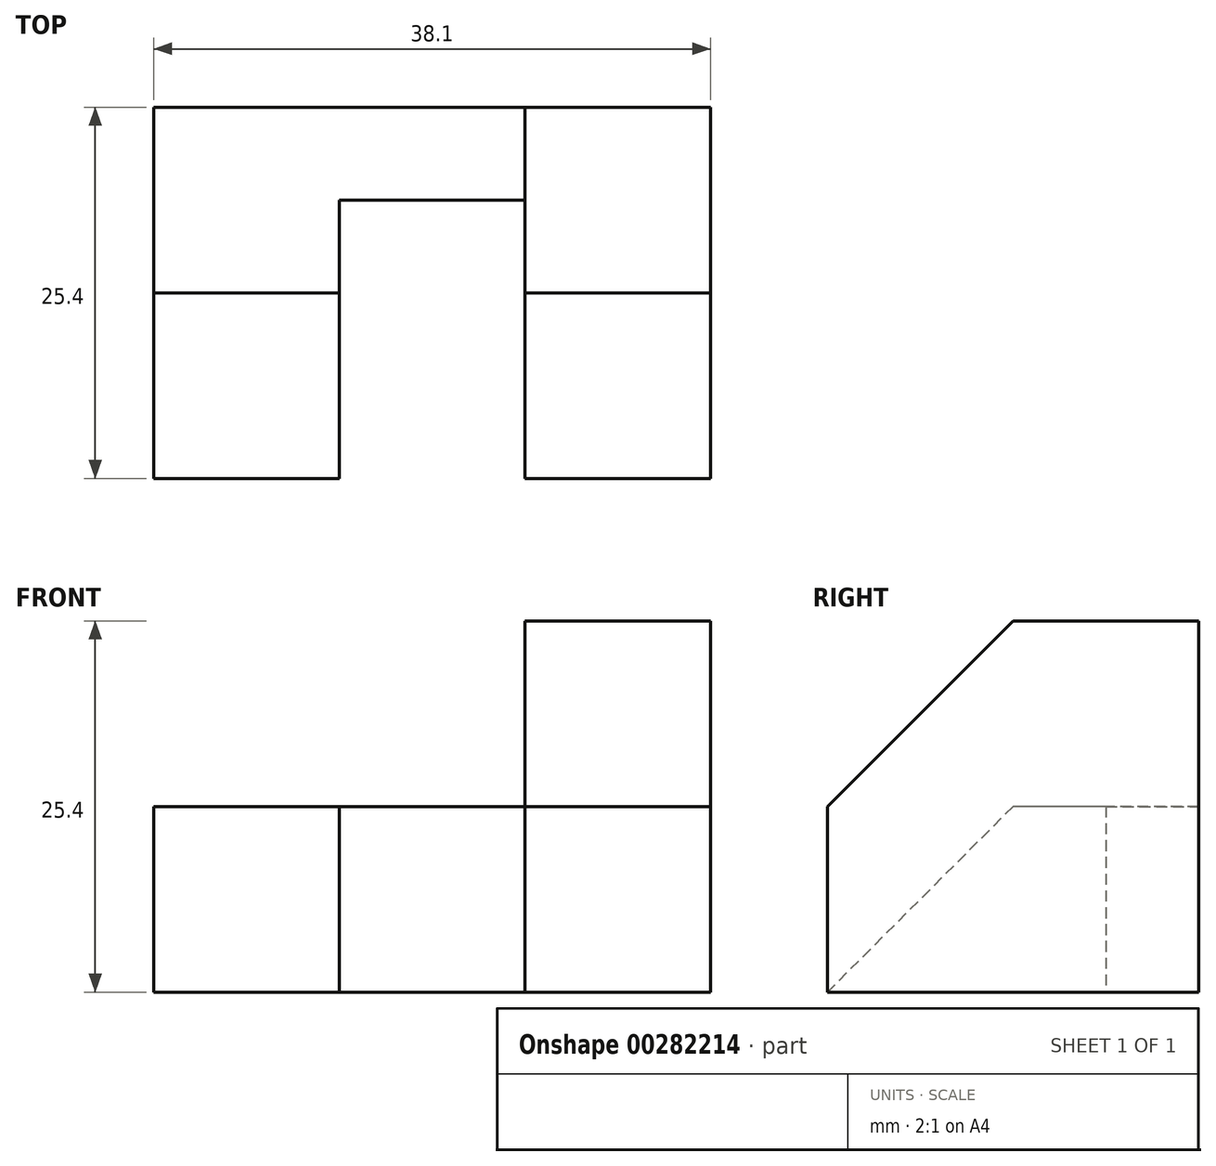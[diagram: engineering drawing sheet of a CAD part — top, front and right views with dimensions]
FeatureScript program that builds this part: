
annotation { "Feature Type Name" : "Feature", "Feature Type Description" : "" }
export const myFeature = defineFeature(function(context is Context, id is Id, definition is map)
    precondition{}
    {
        {
            var Q0;
            Q0=qCreatedBy(makeId("Right.planeOp"),FACE);
            var sketch = newSketch(context, id + "F0", { "sketchPlane" : qUnion([Q0])});
            skLineSegment(sketch, "E0", {"start": v(0, 0) * mm, "end": v(0, 12.7) * mm});
            skLineSegment(sketch, "E1", {"start": v(0, 12.7) * mm, "end": v(-12.7, 12.7) * mm});
            skLineSegment(sketch, "E2", {"start": v(-12.7, 12.7) * mm, "end": v(-25.4, 0) * mm});
            skLineSegment(sketch, "E3", {"start": v(-25.4, 0) * mm, "end": v(0, 0) * mm});
            skSolve(sketch);
        }
        {
            var Q0;
            Q0 = qSketchRegion(id + "F0", true);
            extrude(context, id + "F1", {"entities" : qUnion([Q0]), "depth" : 12.7 * mm});
        }
        {
            var Q0;
            Q0=qCreatedBy(makeId("Front.planeOp"),FACE);
            var sketch = newSketch(context, id + "F2", { "sketchPlane" : qUnion([Q0])});
            skLineSegment(sketch, "E4", {"start": v(12.7, 0) * mm, "end": v(25.4, 0) * mm});
            skLineSegment(sketch, "E5", {"start": v(25.4, 0) * mm, "end": v(25.4, 12.7) * mm});
            skLineSegment(sketch, "E6", {"start": v(25.4, 12.7) * mm, "end": v(12.7, 12.7) * mm});
            skLineSegment(sketch, "E7", {"start": v(12.7, 12.7) * mm, "end": v(12.7, 0) * mm});
            skSolve(sketch);
        }
        {
            var Q0;
            Q0 = qSketchRegion(id + "F2", true);
            extrude(context, id + "F3", {"entities" : qUnion([Q0]), "operationType" : NewBodyOperationType.ADD, "depth" : 6.35 * mm});
        }
        {
            var Q0;
            Q0=makeQuery(id+"F3.opExtrude","SWEPT_FACE",FACE,{"disambiguationData":[OSD([sQuery(id+"F2.wireOp",EDGE,"E5")])]});
            var sketch = newSketch(context, id + "F4", { "sketchPlane" : qUnion([Q0])});
            skLineSegment(sketch, "E8", {"start": v(0, 0) * mm, "end": v(0, 25.4) * mm});
            skLineSegment(sketch, "E9", {"start": v(0, 25.4) * mm, "end": v(-12.7, 25.4) * mm});
            skLineSegment(sketch, "E10", {"start": v(-12.7, 25.4) * mm, "end": v(-25.4, 12.7) * mm});
            skLineSegment(sketch, "E11", {"start": v(-25.4, 12.7) * mm, "end": v(-25.4, 0) * mm});
            skLineSegment(sketch, "E12", {"start": v(-25.4, 0) * mm, "end": v(0, 0) * mm});
            skSolve(sketch);
        }
        {
            var Q0;
            Q0 = qSketchRegion(id + "F4", true);
            extrude(context, id + "F5", {"entities" : qUnion([Q0]), "operationType" : NewBodyOperationType.ADD, "depth" : 12.7 * mm});
        }
    });
